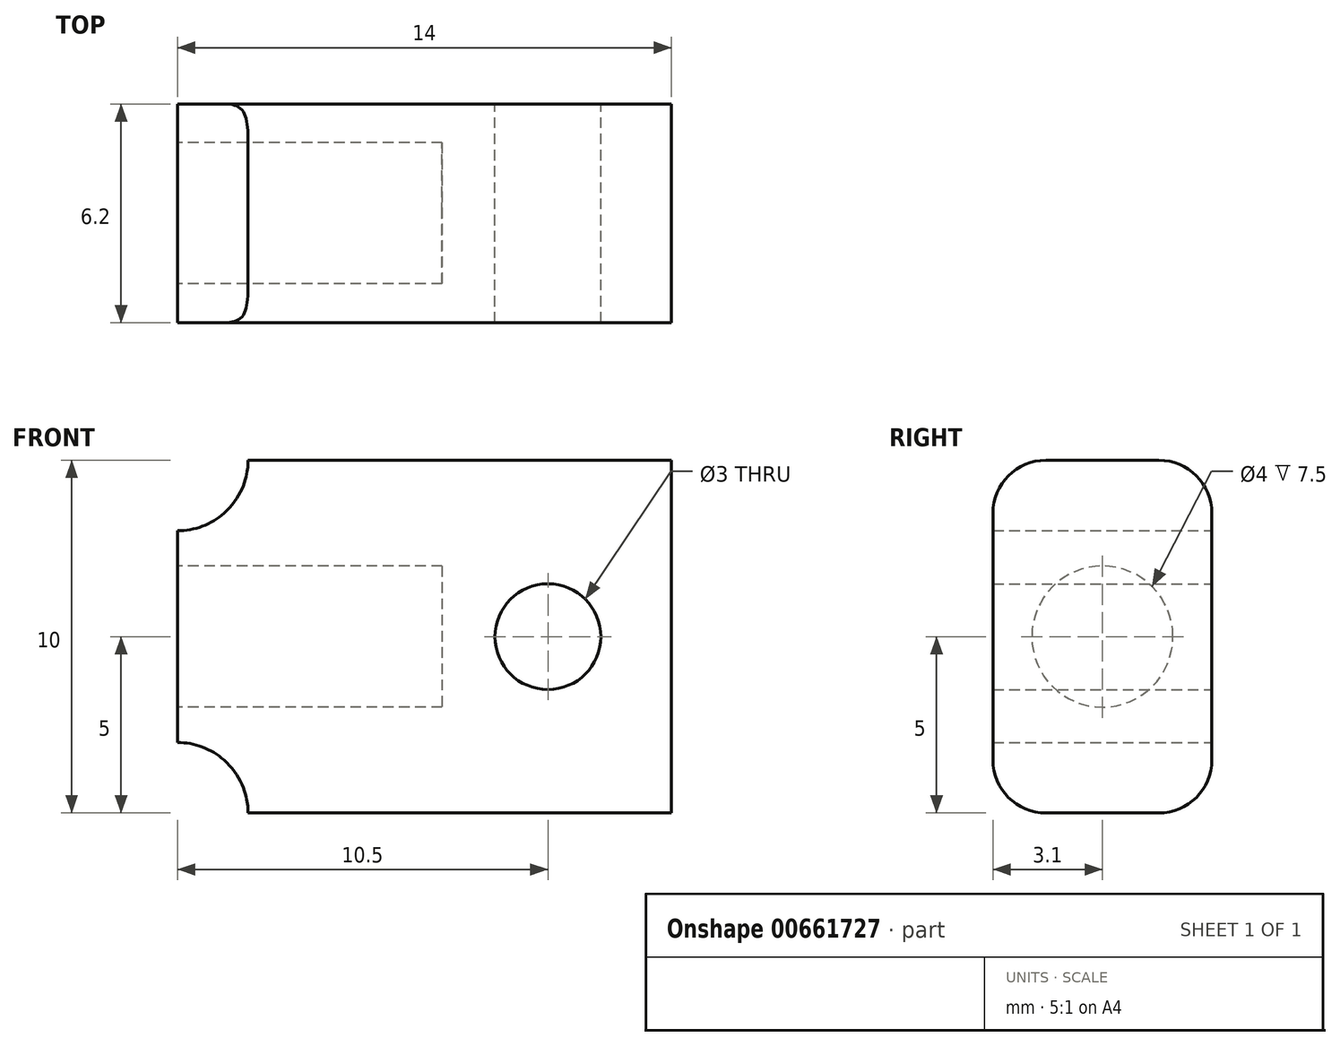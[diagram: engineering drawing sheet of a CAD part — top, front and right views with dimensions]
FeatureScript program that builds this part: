
annotation { "Feature Type Name" : "Feature", "Feature Type Description" : "" }
export const myFeature = defineFeature(function(context is Context, id is Id, definition is map)
    precondition{}
    {
        {
            var Q0;
            Q0=qCreatedBy(makeId("Front.planeOp"),FACE);
            var sketch = newSketch(context, id + "F0", { "sketchPlane" : qUnion([Q0])});
            skLineSegment(sketch, "E0.bottom", {"start": v(0, 0) * mm, "end": v(-12, 0) * mm});
            skLineSegment(sketch, "E0.top", {"start": v(0, 10) * mm, "end": v(-12, 10) * mm});
            skLineSegment(sketch, "E0.left", {"start": v(0, 0) * mm, "end": v(0, 10) * mm});
            skLineSegment(sketch, "E0.right", {"start": v(-14, 2) * mm, "end": v(-14, 8) * mm});
            skArc(sketch, "E1", {"start": v(-14, 8) * mm, "mid": v(-12.59, 8.59) * mm, "end": v(-12, 10) * mm});
            skArc(sketch, "E2", {"start": v(-12, 0) * mm, "mid": v(-12.59, 1.41) * mm, "end": v(-14, 2) * mm});
            skCircle(sketch, "E3", {"center": v(-3.5, 5) * mm, "radius": 1.5 * mm});
            skPoint(sketch, "E3.centerSnap0", {"position": v(0, 5) * mm});
            skSolve(sketch);
        }
        {
            var Q0;
            Q0=makeQuery(id+"F0.imprint","IMPRINT",FACE,{"disambiguationData":[TD([[makeQuery(id+"F0.imprint","IMPRINT",EDGE,{"derivedFrom":sQuery(id+"F0.wireOp",EDGE,"E0.bottom")}),-1.0]])]});
            extrude(context, id + "F1", {"entities" : qUnion([Q0]), "depth" : 6.2 * mm, "offsetDistance" : 25 * mm});
        }
        {
            var Q0;
            Q0=makeQuery(id+"F1.opExtrude","CAP_EDGE",EDGE,{"disambiguationData":[OSD([sQuery(id+"F0.wireOp",EDGE,"E0.top")])],"isStart":false});
            var Q1;
            Q1=makeQuery(id+"F1.opExtrude","CAP_EDGE",EDGE,{"disambiguationData":[OSD([sQuery(id+"F0.wireOp",EDGE,"E0.top")])],"isStart":true});
            var Q2;
            Q2=makeQuery(id+"F1.opExtrude","CAP_EDGE",EDGE,{"disambiguationData":[OSD([sQuery(id+"F0.wireOp",EDGE,"E0.bottom")])],"isStart":true});
            var Q3;
            Q3=makeQuery(id+"F1.opExtrude","CAP_EDGE",EDGE,{"disambiguationData":[OSD([sQuery(id+"F0.wireOp",EDGE,"E0.bottom")])],"isStart":false});
            fillet(context, id + "F2", {"entities" : qUnion([Q0, Q1, Q2, Q3]), "radius" : 1.5 * mm, "tangentPropagation" : true, "allowEdgeOverflow" : false});
        }
        {
            var Q0;
            Q0=makeQuery(id+"F1.opExtrude","SWEPT_FACE",FACE,{"disambiguationData":[OSD([sQuery(id+"F0.wireOp",EDGE,"E0.right")])]});
            var sketch = newSketch(context, id + "F3", { "sketchPlane" : qUnion([Q0])});
            skCircle(sketch, "E4", {"center": v(3.1, 5) * mm, "radius": 2 * mm});
            skPoint(sketch, "E4.centerSnap0", {"position": v(0, 5) * mm});
            skPoint(sketch, "E4.centerSnap1", {"position": v(3.1, 8) * mm});
            skSolve(sketch);
        }
        {
            var Q0;
            Q0 = qSketchRegion(id + "F3", true);
            extrude(context, id + "F4", {"entities" : qUnion([Q0]), "operationType" : NewBodyOperationType.REMOVE, "oppositeDirection" : true, "depth" : 7.5 * mm, "offsetDistance" : 25 * mm});
        }
    });
